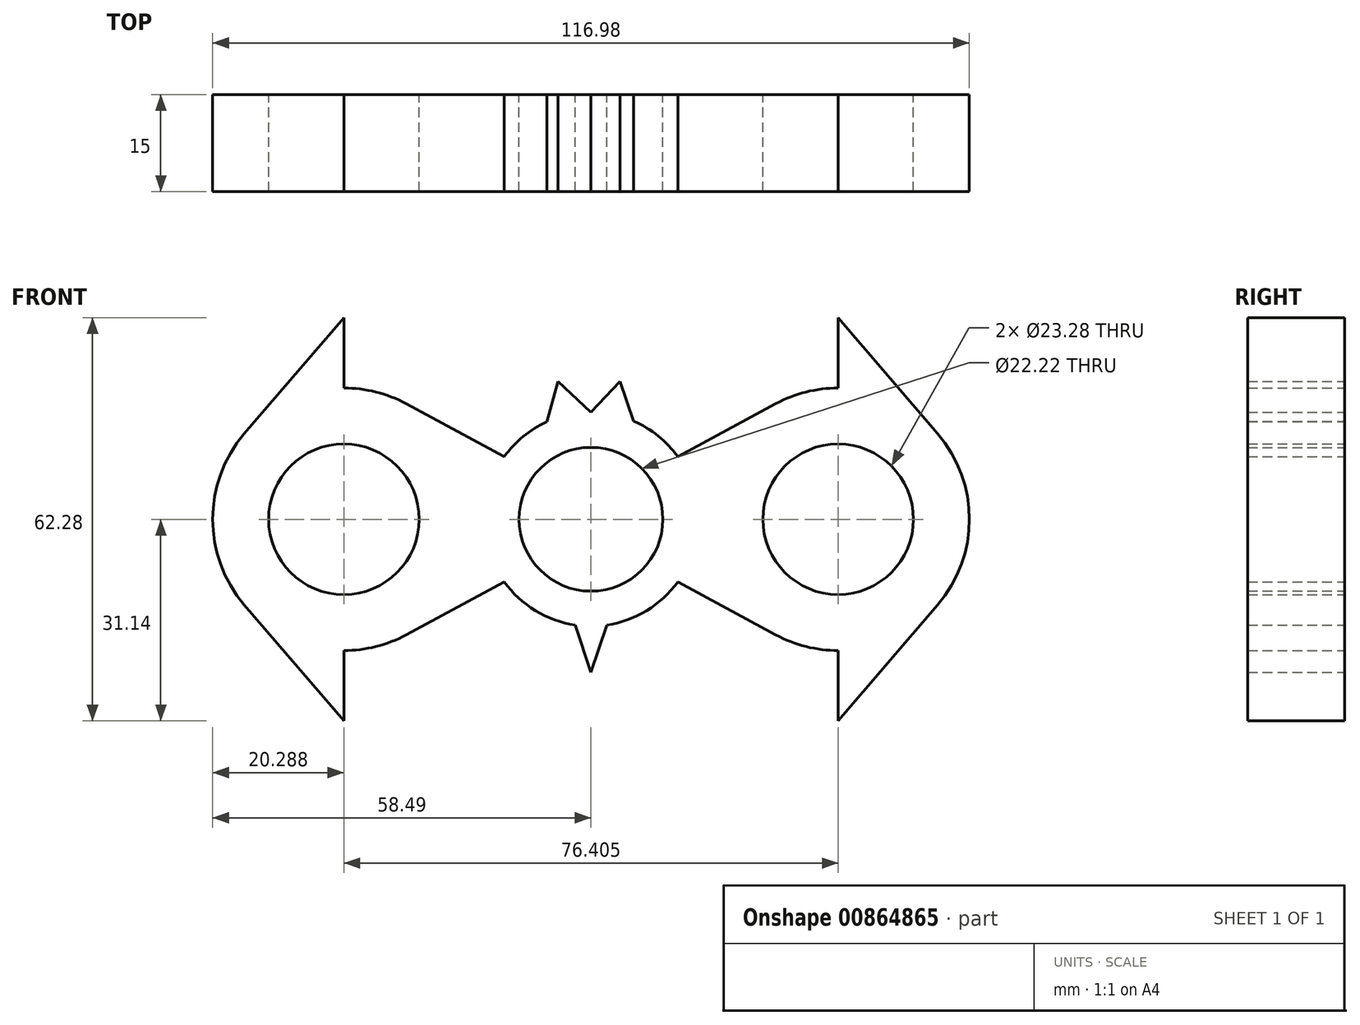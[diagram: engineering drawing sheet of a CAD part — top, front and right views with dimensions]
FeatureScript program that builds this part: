
annotation { "Feature Type Name" : "Feature", "Feature Type Description" : "" }
export const myFeature = defineFeature(function(context is Context, id is Id, definition is map)
    precondition{}
    {
        {
            var Q0;
            Q0=qCreatedBy(makeId("Front.planeOp"),FACE);
            var sketch = newSketch(context, id + "F0", { "sketchPlane" : qUnion([Q0])});
            skLineSegment(sketch, "E0", {"start": v(0, 0) * mm, "end": v(38.2, 0) * mm, "construction": true});
            skLineSegment(sketch, "E1", {"start": v(0, 0) * mm, "end": v(-38.2, 0) * mm, "construction": true});
            skCircle(sketch, "E2", {"center": v(0, 0) * mm, "radius": 11.1 * mm});
            skCircle(sketch, "E3", {"center": v(0, 0) * mm, "radius": 16.53 * mm});
            skCircle(sketch, "E4", {"center": v(38.2, 0) * mm, "radius": 20.29 * mm});
            skCircle(sketch, "E5", {"center": v(-38.2, 0) * mm, "radius": 20.29 * mm});
            skCircle(sketch, "E6", {"center": v(-38.2, 0) * mm, "radius": 11.64 * mm});
            skCircle(sketch, "E7", {"center": v(38.2, 0) * mm, "radius": 11.64 * mm});
            skLineSegment(sketch, "E8", {"start": v(-38.2, 31.14) * mm, "end": v(-38.2, 20.29) * mm, "construction": true});
            skLineSegment(sketch, "E9", {"start": v(-38.2, 20.29) * mm, "end": v(-38.2, -20.29) * mm, "construction": true});
            skLineSegment(sketch, "E10", {"start": v(-38.2, -20.29) * mm, "end": v(-38.2, -31.14) * mm, "construction": true});
            skLineSegment(sketch, "E11", {"start": v(-38.2, 31.14) * mm, "end": v(-53.6, 13.22) * mm});
            skLineSegment(sketch, "E12", {"start": v(-38.2, -31.14) * mm, "end": v(-53.6, -13.22) * mm});
            skLineSegment(sketch, "E13", {"start": v(38.2, 31.14) * mm, "end": v(38.2, -31.14) * mm});
            skLineSegment(sketch, "E14", {"start": v(38.2, 31.14) * mm, "end": v(53.6, 13.22) * mm});
            skLineSegment(sketch, "E15", {"start": v(38.2, -31.14) * mm, "end": v(53.6, -13.22) * mm});
            skLineSegment(sketch, "E16", {"start": v(-28.58, 17.86) * mm, "end": v(-13.4, 9.68) * mm});
            skLineSegment(sketch, "E17", {"start": v(-28.58, -17.86) * mm, "end": v(-13.4, -9.68) * mm});
            skLineSegment(sketch, "E18", {"start": v(28.58, 17.86) * mm, "end": v(13.4, 9.68) * mm});
            skLineSegment(sketch, "E19", {"start": v(28.58, -17.86) * mm, "end": v(13.4, -9.68) * mm});
            skLineSegment(sketch, "E20", {"start": v(-38.2, 31.14) * mm, "end": v(-38.2, -31.14) * mm});
            skLineSegment(sketch, "E21", {"start": v(0, -23.68) * mm, "end": v(0, -16.53) * mm});
            skLineSegment(sketch, "E22", {"start": v(0, -23.68) * mm, "end": v(2.46, -16.35) * mm});
            skLineSegment(sketch, "E23", {"start": v(0, -23.68) * mm, "end": v(-2.46, -16.35) * mm});
            skLineSegment(sketch, "E24", {"start": v(0, 16.53) * mm, "end": v(-5.11, 21.32) * mm});
            skLineSegment(sketch, "E25", {"start": v(-5.11, 21.32) * mm, "end": v(-6.84, 15.05) * mm});
            skLineSegment(sketch, "E26", {"start": v(-6.84, 15.05) * mm, "end": v(0, 16.53) * mm});
            skLineSegment(sketch, "E27", {"start": v(0, 16.53) * mm, "end": v(4.48, 21.32) * mm});
            skLineSegment(sketch, "E28", {"start": v(4.48, 21.32) * mm, "end": v(6.58, 15.17) * mm});
            skSolve(sketch);
        }
        {
            var Q0;
            Q0 = qSketchRegion(id + "F0", true);
            extrude(context, id + "F1", {"entities" : qUnion([Q0]), "depth" : 15 * mm, "offsetDistance" : 25 * mm});
        }
    });
